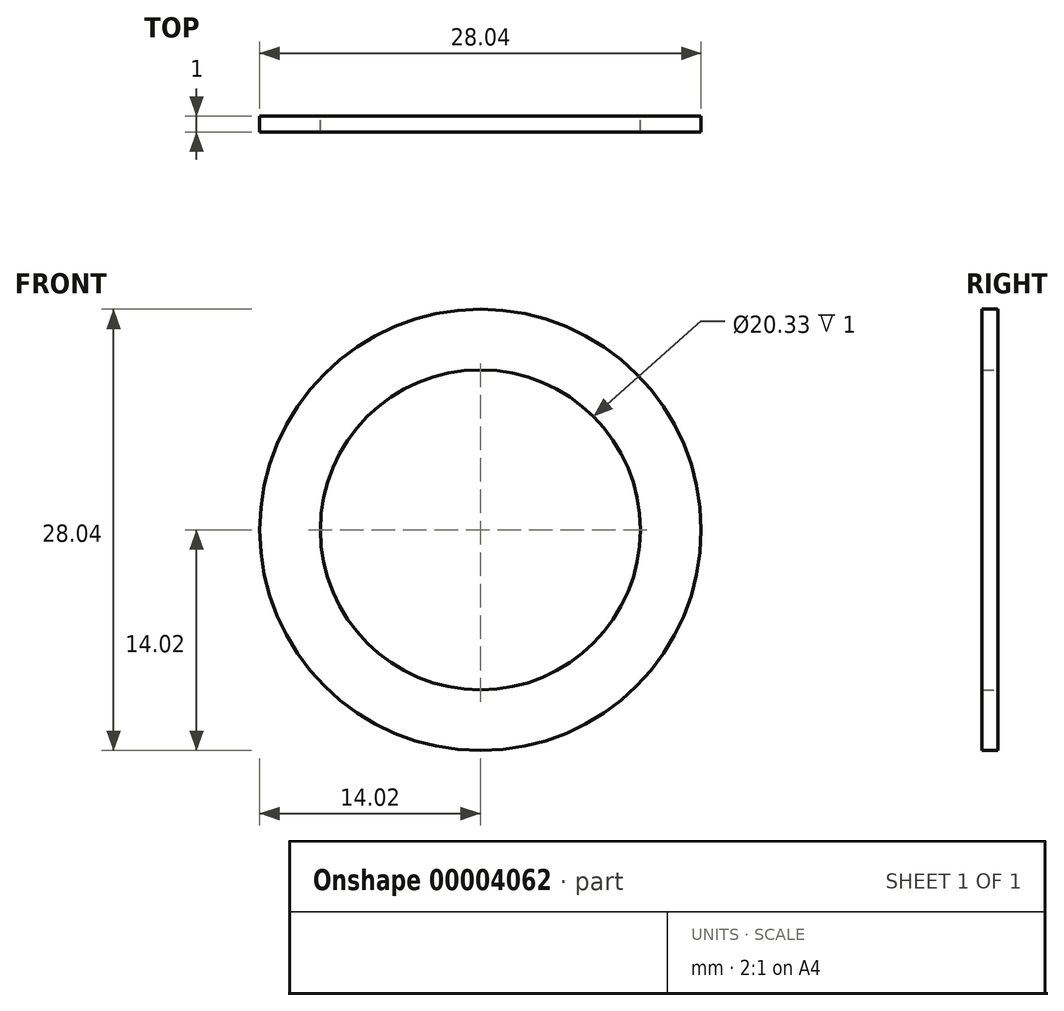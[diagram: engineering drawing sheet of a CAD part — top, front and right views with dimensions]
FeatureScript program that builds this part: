
annotation { "Feature Type Name" : "Feature", "Feature Type Description" : "" }
export const myFeature = defineFeature(function(context is Context, id is Id, definition is map)
    precondition{}
    {
        {
            var Q0;
            Q0=qCreatedBy(makeId("Front.planeOp"),FACE);
            var sketch = newSketch(context, id + "F0", { "sketchPlane" : qUnion([Q0])});
            skCircle(sketch, "E0", {"center": v(0, 0) * mm, "radius": 10.16 * mm});
            skCircle(sketch, "E1", {"center": v(0, 0) * mm, "radius": 12.7 * mm});
            skSolve(sketch);
        }
        {
            var Q0;
            Q0=makeQuery(id+"F0.imprint","IMPRINT",FACE,{"disambiguationData":[TD([[makeQuery(id+"F0.imprint","IMPRINT",EDGE,{"derivedFrom":sQuery(id+"F0.wireOp",EDGE,"E0")}),1.0]])]});
            extrude(context, id + "F1", {"entities" : qUnion([Q0]), "depth" : 1 * mm});
        }
        {
            var Q0;
            Q0=makeQuery(id+"F1.opExtrude","CAP_FACE",FACE,{"disambiguationData":[OSD([sQuery(id+"F0.wireOp",EDGE,"E0")])],"isStart":true});
            var sketch = newSketch(context, id + "F2", { "sketchPlane" : qUnion([Q0])});
            skCircle(sketch, "E2", {"center": v(0, 0) * mm, "radius": 14.02 * mm});
            skSolve(sketch);
        }
        {
            var Q0;
            Q0=makeQuery(id+"F2.imprint","IMPRINT",FACE,{"disambiguationData":[TD([[makeQuery(id+"F2.imprint","IMPRINT",EDGE,{"derivedFrom":sQuery(id+"F2.wireOp",EDGE,"E2")}),1.0]])]});
            extrude(context, id + "F3", {"entities" : qUnion([Q0]), "oppositeDirection" : true, "depth" : 1 * mm});
        }
    });
